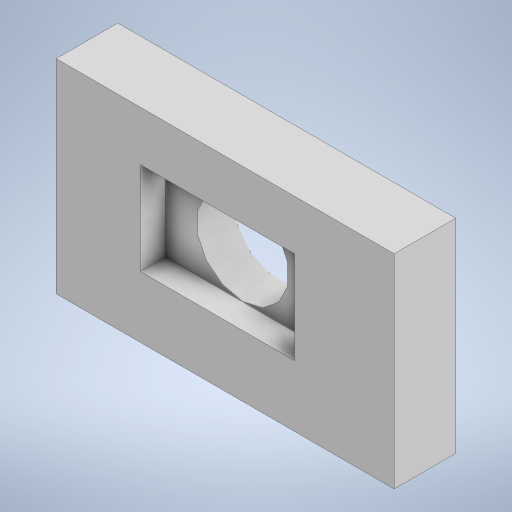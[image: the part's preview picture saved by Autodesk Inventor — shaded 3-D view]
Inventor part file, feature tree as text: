
AUTODESK INVENTOR PART (.ipt)
format: ipt  version: 2023 (Build 270158000, 158)  size: 643,584 bytes
history: native  units: in
note: dims shown in document units (in); Inventor stores cm internally (conversion verified against a paired STEP export)
features: extrude x17, sketch x15, fillet x2
ambient origin geometry x8: Origin, YZ Plane, XZ Plane, XY Plane, X Axis, Y Axis, Z Axis, Center Point
bodies: Solid1 (feature_tree)
feature tree (34):
  extrude  "Extrusion1"  Depth=4.5in
  extrude  "Extrusion2"  Depth=0.2in
  fillet  "Fillet1"  Radius=1.4in
  extrude  "Extrusion3"  Depth=0.25in
  extrude  "Extrusion4"  Depth=2.2875in
  extrude  "Extrusion5"  Depth=0.5437in
  sketch  "Sketch6"  dims[d13=0.75in d14=1.4in d15=0.0in]
  extrude  "Extrusion6"  Depth=1.4in TaperAngle=0.0deg
  extrude  "Extrusion9"  Depth=0.14in
  extrude  "Extrusion10"  Depth=0.275in
  extrude  "Extrusion11"  Depth=0.25in
  extrude  "Extrusion12"  Depth=0.15in
  extrude  "Extrusion13"  Depth=0.7in
  extrude  "Extrusion14"  Depth=0.1in
  extrude  "Extrusion15"  Depth=0.615in
  extrude  "Extrusion16"  Depth=1.1in
  fillet  "Fillet2"  Radius=0.21in
  extrude  "Extrusion17"  Depth=0.5in
  extrude  "Extrusion18"  Depth=0.5in
  extrude  "Extrusion19"  Depth=0.5in
  sketch  "Sketch1"  dims[d0=7.0in d1=4.5in]
  sketch  "Sketch2"  dims[d2=1.5in d3=0.0in d4=0.2in d5=1.4in d6=0.0in]
  sketch  "Sketch3"  dims[d7=0.125in d8=0.25in]
  sketch  "Sketch4"  dims[d9=0.25in d10=2.2875in]
  sketch  "Sketch5"  dims[d11=3.4125in d12=0.5437in]
  sketch  "Sketch8"  dims[d16=0.1in d17=0.14in]
  sketch  "Sketch9"  dims[d18=0.1in d19=0.275in]
  sketch  "Sketch10"  dims[d20=0.35in d21=0.25in]
  sketch  "Sketch11"  dims[d22=0.15in d23=0.15in]
  sketch  "Sketch12"  dims[d24=0.25in d25=0.7in]
  sketch  "Sketch13"  dims[d26=0.1in d27=0.1in]
  sketch  "Sketch14"  dims[d28=0.25in d29=0.615in]
  sketch  "Sketch15"  dims[d30=0.25in d31=1.1in d32=0.21in]
  sketch  "Sketch16"  dims[d33=0.3075in d34=0.5575in d35=1.65in d36=0.3075in d37=0.21in d38=0.5575in d39=2.1in d40=0.1in d41=0.1in d42=0.3in d43=0.1in d44=0.25in d45=0.615in d46=2.4in d47=0.11in d48=2.51in d49=0.5575in d50=0.1in d51=0.615in d52=0.175in d53=0.175in d54=0.1in d55=0.1in d56=0.25in d57=3.15in d58=0.1in d59=0.515in d60=0.05in d61=0.0in d62=0.1562in d63=0.1562in d64=0.2188in d65=0.2188in d66=0.2188in d67=0.2188in d68=0.2188in d69=0.2188in d70=0.625in d71=0.625in d72=0.625in d73=0.625in d74=0.8906in d76=2.25in d77=0.3in d78=0.3in d79=0.3in d80=0.3in d81=0.3in d82=0.625in d83=0.625in d84=0.625in d85=0.625in d86=1.0in d87=3.1in d88=3.1in d89=3.1in d90=3.1in d91=3.1in d92=1.0in d93=0.0in d97=0.4in d98=0.4in d99=0.4in d100=0.4in d101=0.4in d102=0.05in d103=0.0in d119=0.075in d120=0.075in d121=0.075in d122=0.075in d123=0.075in d124=0.0688in d125=0.0in d126=0.25in d127=0.275in d128=0.25in d129=0.25in d130=0.25in d131=2.1in d132=0.125in d133=0.0625in d134=0.05in d135=0.0in d136=0.6in d137=3.35in d139=0.3in d140=0.3155in d141=0.3157in d142=0.0375in d143=0.0in d144=2.0in d145=0.8125in d146=0.0825in d147=0.35in d148=0.15in d149=0.1in d150=0.7in d151=0.2in d152=0.0in d153=0.075in d154=0.125in d155=0.0in d156=0.3in d157=2.5in d158=0.5in d159=0.25in d160=0.0in d161=0.5in d162=0.081in d163=0.0in d164=0.45in d165=0.6in d166=0.2in d167=0.2in d168=0.2in d169=0.075in d170=0.075in d171=0.075in d172=0.075in d173=0.2in d174=0.2in d175=0.2in d176=0.2in d177=0.075in d178=0.0in d179=0.125in d180=0.0375in d181=0.0375in d182=2.0in d183=0.5in d184=0.0in d185=0.0in d187=2.8in d188=5.0in d189=0.0in d190=5.0in d191=0.0in]
